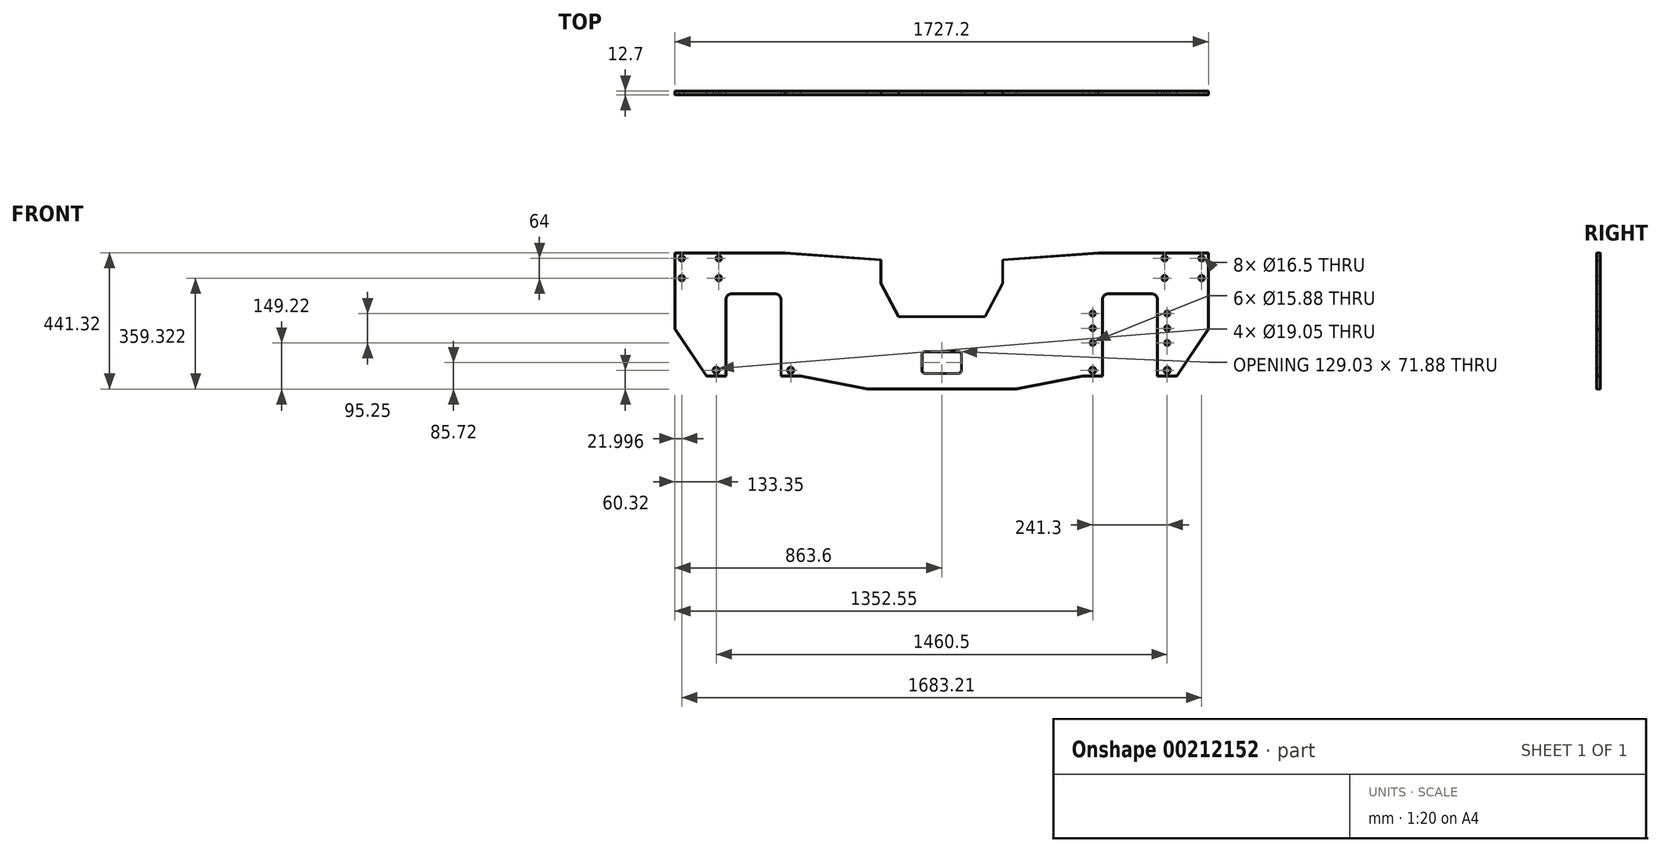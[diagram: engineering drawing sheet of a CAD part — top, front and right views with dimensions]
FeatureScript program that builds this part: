
annotation { "Feature Type Name" : "Feature", "Feature Type Description" : "" }
export const myFeature = defineFeature(function(context is Context, id is Id, definition is map)
    precondition{}
    {
        {
            var Q0;
            Q0=qCreatedBy(makeId("Front.planeOp"),FACE);
            var sketch = newSketch(context, id + "F0", { "sketchPlane" : qUnion([Q0])});
            skLineSegment(sketch, "E0", {"start": v(0, 0) * mm, "end": v(0, 247.15) * mm});
            skLineSegment(sketch, "E1", {"start": v(0, 247.15) * mm, "end": v(355.6, 247.15) * mm});
            skLineSegment(sketch, "E2", {"start": v(355.6, 247.15) * mm, "end": v(666.75, 224.93) * mm});
            skLineSegment(sketch, "E3", {"start": v(666.75, 224.93) * mm, "end": v(666.75, 148.73) * mm});
            skLineSegment(sketch, "E4", {"start": v(666.75, 148.73) * mm, "end": v(723.9, 40.78) * mm});
            skLineSegment(sketch, "E5", {"start": v(723.9, 40.78) * mm, "end": v(863.6, 40.78) * mm});
            skLineSegment(sketch, "E6", {"start": v(0, 0) * mm, "end": v(101.6, -152.9) * mm});
            skLineSegment(sketch, "E7", {"start": v(101.6, -152.9) * mm, "end": v(165.1, -152.9) * mm});
            skLineSegment(sketch, "E8", {"start": v(165.1, -152.9) * mm, "end": v(165.1, 94.75) * mm});
            skLineSegment(sketch, "E9", {"start": v(184.15, 113.8) * mm, "end": v(323.85, 113.8) * mm});
            skLineSegment(sketch, "E10", {"start": v(342.9, 94.75) * mm, "end": v(342.9, -152.9) * mm});
            skLineSegment(sketch, "E11", {"start": v(342.9, -152.9) * mm, "end": v(406.4, -152.9) * mm});
            skLineSegment(sketch, "E12", {"start": v(406.4, -152.9) * mm, "end": v(622.3, -194.17) * mm});
            skLineSegment(sketch, "E13", {"start": v(622.3, -194.17) * mm, "end": v(863.6, -194.17) * mm});
            skLineSegment(sketch, "E14", {"start": v(863.6, -194.17) * mm, "end": v(863.6, 40.78) * mm, "construction": true});
            skPoint(sketch, "E15.visualSharp", {"position": v(342.9, 113.8) * mm});
            skArc(sketch, "E15.filletArc", {"start": v(342.9, 94.75) * mm, "mid": v(337.32, 108.22) * mm, "end": v(323.85, 113.8) * mm});
            skPoint(sketch, "E16.visualSharp", {"position": v(165.1, 113.8) * mm});
            skArc(sketch, "E16.filletArc", {"start": v(184.15, 113.8) * mm, "mid": v(170.68, 108.22) * mm, "end": v(165.1, 94.75) * mm});
            skCircle(sketch, "E17", {"center": v(374.65, -133.85) * mm, "radius": 9.53 * mm});
            skCircle(sketch, "E18", {"center": v(133.35, -133.85) * mm, "radius": 9.53 * mm});
            skCircle(sketch, "E19", {"center": v(374.65, -44.95) * mm, "radius": 7.94 * mm});
            skCircle(sketch, "E20", {"center": v(374.65, 2.68) * mm, "radius": 7.94 * mm});
            skCircle(sketch, "E21", {"center": v(374.65, 50.3) * mm, "radius": 7.94 * mm});
            skCircle(sketch, "E22", {"center": v(133.35, -44.95) * mm, "radius": 7.94 * mm});
            skCircle(sketch, "E23", {"center": v(133.35, 2.68) * mm, "radius": 7.94 * mm});
            skCircle(sketch, "E24", {"center": v(133.35, 50.3) * mm, "radius": 7.94 * mm});
            skLineSegment(sketch, "E25.MirrorCS", {"start": v(1003.3, 40.78) * mm, "end": v(863.6, 40.78) * mm});
            skLineSegment(sketch, "E26.MirrorCS", {"start": v(1104.9, -194.17) * mm, "end": v(863.6, -194.17) * mm});
            skLineSegment(sketch, "E27.MirrorCS", {"start": v(1320.8, -152.9) * mm, "end": v(1104.9, -194.17) * mm});
            skLineSegment(sketch, "E28.MirrorCS", {"start": v(1384.3, -152.9) * mm, "end": v(1320.8, -152.9) * mm});
            skLineSegment(sketch, "E29.MirrorCS", {"start": v(1384.3, 94.75) * mm, "end": v(1384.3, -152.9) * mm});
            skArc(sketch, "E30.MirrorCS", {"start": v(1384.3, 94.75) * mm, "mid": v(1389.88, 108.22) * mm, "end": v(1403.35, 113.8) * mm});
            skLineSegment(sketch, "E31.MirrorCS", {"start": v(1543.05, 113.8) * mm, "end": v(1403.35, 113.8) * mm});
            skArc(sketch, "E32.MirrorCS", {"start": v(1543.05, 113.8) * mm, "mid": v(1556.52, 108.22) * mm, "end": v(1562.1, 94.75) * mm});
            skLineSegment(sketch, "E33.MirrorCS", {"start": v(1562.1, -152.9) * mm, "end": v(1562.1, 94.75) * mm});
            skLineSegment(sketch, "E34.MirrorCS", {"start": v(1625.6, -152.9) * mm, "end": v(1562.1, -152.9) * mm});
            skLineSegment(sketch, "E35.MirrorCS", {"start": v(1727.2, 0) * mm, "end": v(1625.6, -152.9) * mm});
            skLineSegment(sketch, "E36.MirrorCS", {"start": v(1727.2, 0) * mm, "end": v(1727.2, 247.15) * mm});
            skLineSegment(sketch, "E37.MirrorCS", {"start": v(1727.2, 247.15) * mm, "end": v(1371.6, 247.15) * mm});
            skLineSegment(sketch, "E38.MirrorCS", {"start": v(1371.6, 247.15) * mm, "end": v(1060.45, 224.93) * mm});
            skLineSegment(sketch, "E39.MirrorCS", {"start": v(1060.45, 224.93) * mm, "end": v(1060.45, 148.73) * mm});
            skLineSegment(sketch, "E40.MirrorCS", {"start": v(1060.45, 148.73) * mm, "end": v(1003.3, 40.78) * mm});
            skCircle(sketch, "E41.MirrorC", {"center": v(1352.55, -133.85) * mm, "radius": 9.53 * mm});
            skCircle(sketch, "E42.MirrorC", {"center": v(1352.55, -44.95) * mm, "radius": 7.94 * mm});
            skCircle(sketch, "E43.MirrorC", {"center": v(1352.55, 2.68) * mm, "radius": 7.94 * mm});
            skCircle(sketch, "E44.MirrorC", {"center": v(1352.55, 50.3) * mm, "radius": 7.94 * mm});
            skCircle(sketch, "E45.MirrorC", {"center": v(1593.85, 50.3) * mm, "radius": 7.94 * mm});
            skCircle(sketch, "E46.MirrorC", {"center": v(1593.85, 2.68) * mm, "radius": 7.94 * mm});
            skCircle(sketch, "E47.MirrorC", {"center": v(1593.85, -44.95) * mm, "radius": 7.94 * mm});
            skCircle(sketch, "E48.MirrorC", {"center": v(1593.85, -133.85) * mm, "radius": 9.53 * mm});
            skLineSegment(sketch, "E49.bottom", {"start": v(809.63, -73.52) * mm, "end": v(917.58, -73.52) * mm});
            skLineSegment(sketch, "E49.top", {"start": v(809.63, -143.37) * mm, "end": v(917.58, -143.37) * mm});
            skLineSegment(sketch, "E49.left", {"start": v(800.1, -83.05) * mm, "end": v(800.1, -133.85) * mm});
            skLineSegment(sketch, "E49.right", {"start": v(927.1, -83.05) * mm, "end": v(927.1, -133.85) * mm});
            skPoint(sketch, "E49.middle", {"position": v(863.6, -108.45) * mm});
            skPoint(sketch, "E50.visualSharp", {"position": v(800.1, -73.52) * mm});
            skArc(sketch, "E50.filletArc", {"start": v(809.63, -73.52) * mm, "mid": v(802.89, -76.31) * mm, "end": v(800.1, -83.05) * mm});
            skPoint(sketch, "E51.visualSharp", {"position": v(927.1, -73.52) * mm});
            skArc(sketch, "E51.filletArc", {"start": v(927.1, -83.05) * mm, "mid": v(924.31, -76.31) * mm, "end": v(917.58, -73.52) * mm});
            skPoint(sketch, "E52.visualSharp", {"position": v(927.1, -143.37) * mm});
            skArc(sketch, "E52.filletArc", {"start": v(917.58, -143.37) * mm, "mid": v(924.31, -140.58) * mm, "end": v(927.1, -133.85) * mm});
            skPoint(sketch, "E53.visualSharp", {"position": v(800.1, -143.37) * mm});
            skArc(sketch, "E53.filletArc", {"start": v(800.1, -133.85) * mm, "mid": v(802.89, -140.58) * mm, "end": v(809.63, -143.37) * mm});
            skCircle(sketch, "E54", {"center": v(22, 229.15) * mm, "radius": 8.25 * mm});
            skCircle(sketch, "E55", {"center": v(141.99, 229.15) * mm, "radius": 8.25 * mm});
            skCircle(sketch, "E56", {"center": v(141.99, 165.15) * mm, "radius": 8.25 * mm});
            skCircle(sketch, "E57", {"center": v(22, 165.15) * mm, "radius": 8.25 * mm});
            skCircle(sketch, "E58.MirrorC", {"center": v(1585.21, 229.15) * mm, "radius": 8.25 * mm});
            skCircle(sketch, "E59.MirrorC", {"center": v(1585.21, 165.15) * mm, "radius": 8.25 * mm});
            skCircle(sketch, "E60.MirrorC", {"center": v(1705.2, 165.15) * mm, "radius": 8.25 * mm});
            skCircle(sketch, "E61.MirrorC", {"center": v(1705.2, 229.15) * mm, "radius": 8.25 * mm});
            skLineSegment(sketch, "E62.0", {"start": v(1050.13, -194.17) * mm, "end": v(1050.13, 40.78) * mm, "construction": true});
            skLineSegment(sketch, "E63.0", {"start": v(677.07, -194.17) * mm, "end": v(677.07, 40.78) * mm, "construction": true});
            skLineSegment(sketch, "E64", {"start": v(677.07, -194.17) * mm, "end": v(1050.13, 40.78) * mm, "construction": true});
            skLineSegment(sketch, "E65", {"start": v(863.6, -76.7) * mm, "end": v(1050.13, -76.7) * mm, "construction": true});
            skLineSegment(sketch, "E66", {"start": v(863.6, -76.7) * mm, "end": v(677.07, -76.7) * mm, "construction": true});
            skSolve(sketch);
        }
        {
            var Q0;
            Q0=makeQuery(id+"F0.imprint","IMPRINT",FACE,{"disambiguationData":[TD([[makeQuery(id+"F0.imprint","IMPRINT",EDGE,{"derivedFrom":sQuery(id+"F0.wireOp",EDGE,"E0")}),-1.0]])]});
            var Q1;
            Q1=makeQuery(id+"F0.imprint","IMPRINT",FACE,{"disambiguationData":[TD([[makeQuery(id+"F0.imprint","IMPRINT",EDGE,{"derivedFrom":sQuery(id+"F0.wireOp",EDGE,"E47.MirrorC")}),-1.0]])]});
            var Q2;
            Q2=makeQuery(id+"F0.imprint","IMPRINT",FACE,{"disambiguationData":[TD([[makeQuery(id+"F0.imprint","IMPRINT",EDGE,{"derivedFrom":sQuery(id+"F0.wireOp",EDGE,"E46.MirrorC")}),-1.0]])]});
            var Q3;
            Q3=makeQuery(id+"F0.imprint","IMPRINT",FACE,{"disambiguationData":[TD([[makeQuery(id+"F0.imprint","IMPRINT",EDGE,{"derivedFrom":sQuery(id+"F0.wireOp",EDGE,"E45.MirrorC")}),-1.0]])]});
            var Q4;
            Q4=makeQuery(id+"F0.imprint","IMPRINT",FACE,{"disambiguationData":[TD([[makeQuery(id+"F0.imprint","IMPRINT",EDGE,{"derivedFrom":sQuery(id+"F0.wireOp",EDGE,"E44.MirrorC")}),-1.0]])]});
            var Q5;
            Q5=makeQuery(id+"F0.imprint","IMPRINT",FACE,{"disambiguationData":[TD([[makeQuery(id+"F0.imprint","IMPRINT",EDGE,{"derivedFrom":sQuery(id+"F0.wireOp",EDGE,"E43.MirrorC")}),-1.0]])]});
            var Q6;
            Q6=makeQuery(id+"F0.imprint","IMPRINT",FACE,{"disambiguationData":[TD([[makeQuery(id+"F0.imprint","IMPRINT",EDGE,{"derivedFrom":sQuery(id+"F0.wireOp",EDGE,"E42.MirrorC")}),-1.0]])]});
            var Q7;
            Q7=makeQuery(id+"F0.imprint","IMPRINT",FACE,{"disambiguationData":[TD([[makeQuery(id+"F0.imprint","IMPRINT",EDGE,{"derivedFrom":sQuery(id+"F0.wireOp",EDGE,"E20")}),1.0]])]});
            var Q8;
            Q8=makeQuery(id+"F0.imprint","IMPRINT",FACE,{"disambiguationData":[TD([[makeQuery(id+"F0.imprint","IMPRINT",EDGE,{"derivedFrom":sQuery(id+"F0.wireOp",EDGE,"E21")}),1.0]])]});
            var Q9;
            Q9=makeQuery(id+"F0.imprint","IMPRINT",FACE,{"disambiguationData":[TD([[makeQuery(id+"F0.imprint","IMPRINT",EDGE,{"derivedFrom":sQuery(id+"F0.wireOp",EDGE,"E19")}),1.0]])]});
            var Q10;
            Q10=makeQuery(id+"F0.imprint","IMPRINT",FACE,{"disambiguationData":[TD([[makeQuery(id+"F0.imprint","IMPRINT",EDGE,{"derivedFrom":sQuery(id+"F0.wireOp",EDGE,"E24")}),1.0]])]});
            var Q11;
            Q11=makeQuery(id+"F0.imprint","IMPRINT",FACE,{"disambiguationData":[TD([[makeQuery(id+"F0.imprint","IMPRINT",EDGE,{"derivedFrom":sQuery(id+"F0.wireOp",EDGE,"E23")}),1.0]])]});
            var Q12;
            Q12=makeQuery(id+"F0.imprint","IMPRINT",FACE,{"disambiguationData":[TD([[makeQuery(id+"F0.imprint","IMPRINT",EDGE,{"derivedFrom":sQuery(id+"F0.wireOp",EDGE,"E22")}),1.0]])]});
            extrude(context, id + "F1", {"entities" : qUnion([Q0, Q1, Q2, Q3, Q4, Q5, Q6, Q7, Q8, Q9, Q10, Q11, Q12]), "depth" : 12.7 * mm});
        }
        {
            var Q0;
            Q0=makeQuery(id+"F1.opExtrude","CAP_FACE",FACE,{"disambiguationData":[OSD([sQuery(id+"F0.wireOp",EDGE,"E0"),sQuery(id+"F0.wireOp",EDGE,"E1"),sQuery(id+"F0.wireOp",EDGE,"E2"),sQuery(id+"F0.wireOp",EDGE,"E3"),sQuery(id+"F0.wireOp",EDGE,"E4"),sQuery(id+"F0.wireOp",EDGE,"E5"),sQuery(id+"F0.wireOp",EDGE,"E6"),sQuery(id+"F0.wireOp",EDGE,"E7"),sQuery(id+"F0.wireOp",EDGE,"E8"),sQuery(id+"F0.wireOp",EDGE,"E9"),sQuery(id+"F0.wireOp",EDGE,"E10"),sQuery(id+"F0.wireOp",EDGE,"E11"),sQuery(id+"F0.wireOp",EDGE,"E12"),sQuery(id+"F0.wireOp",EDGE,"E13"),sQuery(id+"F0.wireOp",EDGE,"E15.filletArc"),sQuery(id+"F0.wireOp",EDGE,"E16.filletArc"),sQuery(id+"F0.wireOp",EDGE,"E17"),sQuery(id+"F0.wireOp",EDGE,"E18"),sQuery(id+"F0.wireOp",EDGE,"E19"),sQuery(id+"F0.wireOp",EDGE,"E20"),sQuery(id+"F0.wireOp",EDGE,"E21"),sQuery(id+"F0.wireOp",EDGE,"E22"),sQuery(id+"F0.wireOp",EDGE,"E23"),sQuery(id+"F0.wireOp",EDGE,"E24"),sQuery(id+"F0.wireOp",EDGE,"E25.MirrorCS"),sQuery(id+"F0.wireOp",EDGE,"E26.MirrorCS"),sQuery(id+"F0.wireOp",EDGE,"E27.MirrorCS"),sQuery(id+"F0.wireOp",EDGE,"E28.MirrorCS"),sQuery(id+"F0.wireOp",EDGE,"E29.MirrorCS"),sQuery(id+"F0.wireOp",EDGE,"E30.MirrorCS"),sQuery(id+"F0.wireOp",EDGE,"E31.MirrorCS"),sQuery(id+"F0.wireOp",EDGE,"E32.MirrorCS"),sQuery(id+"F0.wireOp",EDGE,"E33.MirrorCS"),sQuery(id+"F0.wireOp",EDGE,"E34.MirrorCS"),sQuery(id+"F0.wireOp",EDGE,"E35.MirrorCS"),sQuery(id+"F0.wireOp",EDGE,"E36.MirrorCS"),sQuery(id+"F0.wireOp",EDGE,"E37.MirrorCS"),sQuery(id+"F0.wireOp",EDGE,"E38.MirrorCS"),sQuery(id+"F0.wireOp",EDGE,"E39.MirrorCS"),sQuery(id+"F0.wireOp",EDGE,"E40.MirrorCS"),sQuery(id+"F0.wireOp",EDGE,"E41.MirrorC"),sQuery(id+"F0.wireOp",EDGE,"E42.MirrorC"),sQuery(id+"F0.wireOp",EDGE,"E43.MirrorC"),sQuery(id+"F0.wireOp",EDGE,"E44.MirrorC"),sQuery(id+"F0.wireOp",EDGE,"E45.MirrorC"),sQuery(id+"F0.wireOp",EDGE,"E46.MirrorC"),sQuery(id+"F0.wireOp",EDGE,"E47.MirrorC"),sQuery(id+"F0.wireOp",EDGE,"E48.MirrorC"),sQuery(id+"F0.wireOp",EDGE,"E49.bottom"),sQuery(id+"F0.wireOp",EDGE,"E49.top"),sQuery(id+"F0.wireOp",EDGE,"E49.left"),sQuery(id+"F0.wireOp",EDGE,"E49.right"),sQuery(id+"F0.wireOp",EDGE,"E50.filletArc"),sQuery(id+"F0.wireOp",EDGE,"E51.filletArc"),sQuery(id+"F0.wireOp",EDGE,"E52.filletArc"),sQuery(id+"F0.wireOp",EDGE,"E53.filletArc"),sQuery(id+"F0.wireOp",EDGE,"E54"),sQuery(id+"F0.wireOp",EDGE,"E55"),sQuery(id+"F0.wireOp",EDGE,"E56"),sQuery(id+"F0.wireOp",EDGE,"E57"),sQuery(id+"F0.wireOp",EDGE,"E58.MirrorC"),sQuery(id+"F0.wireOp",EDGE,"E59.MirrorC"),sQuery(id+"F0.wireOp",EDGE,"E60.MirrorC"),sQuery(id+"F0.wireOp",EDGE,"E61.MirrorC")])],"isStart":false});
            var Q1;
            Q1=makeQuery(id+"F1.opExtrude","CAP_FACE",FACE,{"disambiguationData":[OSD([sQuery(id+"F0.wireOp",EDGE,"E0"),sQuery(id+"F0.wireOp",EDGE,"E1"),sQuery(id+"F0.wireOp",EDGE,"E2"),sQuery(id+"F0.wireOp",EDGE,"E3"),sQuery(id+"F0.wireOp",EDGE,"E4"),sQuery(id+"F0.wireOp",EDGE,"E5"),sQuery(id+"F0.wireOp",EDGE,"E6"),sQuery(id+"F0.wireOp",EDGE,"E7"),sQuery(id+"F0.wireOp",EDGE,"E8"),sQuery(id+"F0.wireOp",EDGE,"E9"),sQuery(id+"F0.wireOp",EDGE,"E10"),sQuery(id+"F0.wireOp",EDGE,"E11"),sQuery(id+"F0.wireOp",EDGE,"E12"),sQuery(id+"F0.wireOp",EDGE,"E13"),sQuery(id+"F0.wireOp",EDGE,"E15.filletArc"),sQuery(id+"F0.wireOp",EDGE,"E16.filletArc"),sQuery(id+"F0.wireOp",EDGE,"E17"),sQuery(id+"F0.wireOp",EDGE,"E18"),sQuery(id+"F0.wireOp",EDGE,"E19"),sQuery(id+"F0.wireOp",EDGE,"E20"),sQuery(id+"F0.wireOp",EDGE,"E21"),sQuery(id+"F0.wireOp",EDGE,"E22"),sQuery(id+"F0.wireOp",EDGE,"E23"),sQuery(id+"F0.wireOp",EDGE,"E24"),sQuery(id+"F0.wireOp",EDGE,"E25.MirrorCS"),sQuery(id+"F0.wireOp",EDGE,"E26.MirrorCS"),sQuery(id+"F0.wireOp",EDGE,"E27.MirrorCS"),sQuery(id+"F0.wireOp",EDGE,"E28.MirrorCS"),sQuery(id+"F0.wireOp",EDGE,"E29.MirrorCS"),sQuery(id+"F0.wireOp",EDGE,"E30.MirrorCS"),sQuery(id+"F0.wireOp",EDGE,"E31.MirrorCS"),sQuery(id+"F0.wireOp",EDGE,"E32.MirrorCS"),sQuery(id+"F0.wireOp",EDGE,"E33.MirrorCS"),sQuery(id+"F0.wireOp",EDGE,"E34.MirrorCS"),sQuery(id+"F0.wireOp",EDGE,"E35.MirrorCS"),sQuery(id+"F0.wireOp",EDGE,"E36.MirrorCS"),sQuery(id+"F0.wireOp",EDGE,"E37.MirrorCS"),sQuery(id+"F0.wireOp",EDGE,"E38.MirrorCS"),sQuery(id+"F0.wireOp",EDGE,"E39.MirrorCS"),sQuery(id+"F0.wireOp",EDGE,"E40.MirrorCS"),sQuery(id+"F0.wireOp",EDGE,"E41.MirrorC"),sQuery(id+"F0.wireOp",EDGE,"E42.MirrorC"),sQuery(id+"F0.wireOp",EDGE,"E43.MirrorC"),sQuery(id+"F0.wireOp",EDGE,"E44.MirrorC"),sQuery(id+"F0.wireOp",EDGE,"E45.MirrorC"),sQuery(id+"F0.wireOp",EDGE,"E46.MirrorC"),sQuery(id+"F0.wireOp",EDGE,"E47.MirrorC"),sQuery(id+"F0.wireOp",EDGE,"E48.MirrorC"),sQuery(id+"F0.wireOp",EDGE,"E49.bottom"),sQuery(id+"F0.wireOp",EDGE,"E49.top"),sQuery(id+"F0.wireOp",EDGE,"E49.left"),sQuery(id+"F0.wireOp",EDGE,"E49.right"),sQuery(id+"F0.wireOp",EDGE,"E50.filletArc"),sQuery(id+"F0.wireOp",EDGE,"E51.filletArc"),sQuery(id+"F0.wireOp",EDGE,"E52.filletArc"),sQuery(id+"F0.wireOp",EDGE,"E53.filletArc"),sQuery(id+"F0.wireOp",EDGE,"E54"),sQuery(id+"F0.wireOp",EDGE,"E55"),sQuery(id+"F0.wireOp",EDGE,"E56"),sQuery(id+"F0.wireOp",EDGE,"E57"),sQuery(id+"F0.wireOp",EDGE,"E58.MirrorC"),sQuery(id+"F0.wireOp",EDGE,"E59.MirrorC"),sQuery(id+"F0.wireOp",EDGE,"E60.MirrorC"),sQuery(id+"F0.wireOp",EDGE,"E61.MirrorC")])],"isStart":true});
            chamfer(context, id + "F2", {"entities" : qUnion([Q0, Q1]), "width" : 1.02 * mm, "tangentPropagation" : true});
        }
        {
            var Q0;
            Q0=makeQuery(id+"F1.opExtrude","CAP_FACE",FACE,{"disambiguationData":[OSD([sQuery(id+"F0.wireOp",EDGE,"E0"),sQuery(id+"F0.wireOp",EDGE,"E1"),sQuery(id+"F0.wireOp",EDGE,"E2"),sQuery(id+"F0.wireOp",EDGE,"E3"),sQuery(id+"F0.wireOp",EDGE,"E4"),sQuery(id+"F0.wireOp",EDGE,"E5"),sQuery(id+"F0.wireOp",EDGE,"E6"),sQuery(id+"F0.wireOp",EDGE,"E7"),sQuery(id+"F0.wireOp",EDGE,"E8"),sQuery(id+"F0.wireOp",EDGE,"E9"),sQuery(id+"F0.wireOp",EDGE,"E10"),sQuery(id+"F0.wireOp",EDGE,"E11"),sQuery(id+"F0.wireOp",EDGE,"E12"),sQuery(id+"F0.wireOp",EDGE,"E13"),sQuery(id+"F0.wireOp",EDGE,"E15.filletArc"),sQuery(id+"F0.wireOp",EDGE,"E16.filletArc"),sQuery(id+"F0.wireOp",EDGE,"E17"),sQuery(id+"F0.wireOp",EDGE,"E18"),sQuery(id+"F0.wireOp",EDGE,"E25.MirrorCS"),sQuery(id+"F0.wireOp",EDGE,"E26.MirrorCS"),sQuery(id+"F0.wireOp",EDGE,"E27.MirrorCS"),sQuery(id+"F0.wireOp",EDGE,"E28.MirrorCS"),sQuery(id+"F0.wireOp",EDGE,"E29.MirrorCS"),sQuery(id+"F0.wireOp",EDGE,"E30.MirrorCS"),sQuery(id+"F0.wireOp",EDGE,"E31.MirrorCS"),sQuery(id+"F0.wireOp",EDGE,"E32.MirrorCS"),sQuery(id+"F0.wireOp",EDGE,"E33.MirrorCS"),sQuery(id+"F0.wireOp",EDGE,"E34.MirrorCS"),sQuery(id+"F0.wireOp",EDGE,"E35.MirrorCS"),sQuery(id+"F0.wireOp",EDGE,"E36.MirrorCS"),sQuery(id+"F0.wireOp",EDGE,"E37.MirrorCS"),sQuery(id+"F0.wireOp",EDGE,"E38.MirrorCS"),sQuery(id+"F0.wireOp",EDGE,"E39.MirrorCS"),sQuery(id+"F0.wireOp",EDGE,"E40.MirrorCS"),sQuery(id+"F0.wireOp",EDGE,"E41.MirrorC"),sQuery(id+"F0.wireOp",EDGE,"E48.MirrorC"),sQuery(id+"F0.wireOp",EDGE,"E49.bottom"),sQuery(id+"F0.wireOp",EDGE,"E49.top"),sQuery(id+"F0.wireOp",EDGE,"E49.left"),sQuery(id+"F0.wireOp",EDGE,"E49.right"),sQuery(id+"F0.wireOp",EDGE,"E50.filletArc"),sQuery(id+"F0.wireOp",EDGE,"E51.filletArc"),sQuery(id+"F0.wireOp",EDGE,"E52.filletArc"),sQuery(id+"F0.wireOp",EDGE,"E53.filletArc"),sQuery(id+"F0.wireOp",EDGE,"E54"),sQuery(id+"F0.wireOp",EDGE,"E55"),sQuery(id+"F0.wireOp",EDGE,"E56"),sQuery(id+"F0.wireOp",EDGE,"E57"),sQuery(id+"F0.wireOp",EDGE,"E58.MirrorC"),sQuery(id+"F0.wireOp",EDGE,"E59.MirrorC"),sQuery(id+"F0.wireOp",EDGE,"E60.MirrorC"),sQuery(id+"F0.wireOp",EDGE,"E61.MirrorC")])],"isStart":false});
            var sketch = newSketch(context, id + "F3", { "sketchPlane" : qUnion([Q0])});
            skLineSegment(sketch, "E67", {"start": v(254, -152.9) * mm, "end": v(254, 107.04) * mm, "construction": true});
            skLineSegment(sketch, "E68", {"start": v(254, 18.55) * mm, "end": v(63.5, 18.55) * mm, "construction": true});
            skLineSegment(sketch, "E69", {"start": v(254, 18.55) * mm, "end": v(1473.2, 18.55) * mm, "construction": true});
            skLineSegment(sketch, "E70", {"start": v(1473.2, -152.9) * mm, "end": v(1473.2, 18.55) * mm, "construction": true});
            skLineSegment(sketch, "E71", {"start": v(1473.2, 18.55) * mm, "end": v(1663.7, 18.55) * mm, "construction": true});
            skLineSegment(sketch, "E72.0", {"start": v(343.92, -152.9) * mm, "end": v(164.08, -152.9) * mm, "construction": true});
            skLineSegment(sketch, "E73.0", {"start": v(666.75, 225) * mm, "end": v(1060.45, 225) * mm, "construction": true});
            skLineSegment(sketch, "E74.0", {"start": v(666.75, 225) * mm, "end": v(666.75, 186.9) * mm, "construction": true});
            skLineSegment(sketch, "E75.0", {"start": v(1060.45, 225) * mm, "end": v(1060.45, 186.9) * mm, "construction": true});
            skLineSegment(sketch, "E76", {"start": v(666.75, 186.9) * mm, "end": v(657.23, 186.9) * mm, "construction": true});
            skLineSegment(sketch, "E77", {"start": v(1060.45, 186.9) * mm, "end": v(1069.98, 186.9) * mm, "construction": true});
            skLineSegment(sketch, "E78.0", {"start": v(723.8, 40.78) * mm, "end": v(1003.4, 40.78) * mm, "construction": true});
            skLineSegment(sketch, "E79.0", {"start": v(723.8, 40.78) * mm, "end": v(723.8, -34.22) * mm, "construction": true});
            skPoint(sketch, "E80.orphan", {"position": v(723.29, 40.78) * mm});
            skLineSegment(sketch, "E81.0", {"start": v(1003.4, 40.78) * mm, "end": v(1003.4, -34.22) * mm, "construction": true});
            skLineSegment(sketch, "E82.0", {"start": v(444.5, -152.9) * mm, "end": v(444.5, 107.04) * mm, "construction": true});
            skLineSegment(sketch, "E83.0", {"start": v(1282.7, -152.9) * mm, "end": v(1282.7, 18.55) * mm, "construction": true});
            skPoint(sketch, "E84", {"position": v(444.5, 18.55) * mm});
            skSolve(sketch);
        }
    });
